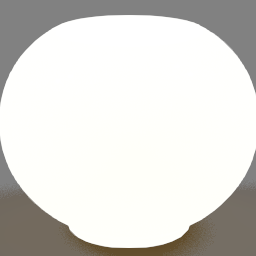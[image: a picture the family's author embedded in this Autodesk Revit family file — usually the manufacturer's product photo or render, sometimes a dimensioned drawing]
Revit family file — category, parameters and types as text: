
# Revit family: 3-5052-xx-xx Axiom Wall Sconce
name_source: partatom
category: Luminarias
units: mm (PartAtom-declared; Revit-internal decimal feet)

## family parameters
Anfitrión = Muro
Compartido = No
Corte con vacíos al cargar = No
Cota de conector redondo = Diámetro de uso
Número OmniClass = 23.80.70.00
Origen de luz = Sí
Punto de cálculo de habitación = No
Siempre vertical = Sí
Tipo de pieza = Normal
Título OmniClass = Lighting

## types (2) — shared parameters
Archivo de red fotométrica = 3-5052-15 Axiom 3LT.ies
Cambio de temperatura de color de luz atenuada = <Ninguno>
Comentarios de vataje = 1 x 11.0 W at 120 V
Diffuser = Ice Acrylic
Fabricante = Oxygen Lighting and Fans
Filtro de color = 16777215
Lámpara = LED Array
Modelo = 3-5052-xx / Axiom Wall Sconce
References = Ref. 3 = 120 V / Ref. 37 = 277 V
URL = www.oxygenlighting.com
Voltage = 120 V
Voltage Input = 120 V or 277 V - 50/60 Hz
Ángulo de inclinación = 90.00°
zero-valued in all types: Elevación por defecto

## per-type parameters (varying)
| type | Metal Finish 1 |
| 3-5052-15 / Black - ice acrylic | 15 - Black |
| 3-5052-40 / Aged Brass - Ice Acrylic | 40 - Aged Brass |

## geometry (parser evidence)
native form markers: Sweep x4
no freeform markers — native parametric forms only
